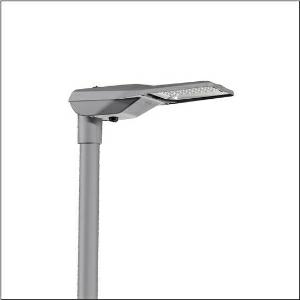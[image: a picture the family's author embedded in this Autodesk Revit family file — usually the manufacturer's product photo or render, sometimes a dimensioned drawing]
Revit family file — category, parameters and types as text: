
# Revit family: streetlight_sl_21_iq_mini___stw1_0a_5xe2e31y08gb_7efe
name_source: partatom
category: Lighting Fixtures
units: mm (PartAtom-declared; Revit-internal decimal feet)

## family parameters
Cut with Voids When Loaded = No
Host = Face
Light Source = No
Part Type = Normal
Room Calculation Point = No
Round Connector Dimension = Use Diameter
Shared = No

## types (1)
- --- (1 x LED, 5990 lm, 39.8 W, 3000K)
    Apparent Load = 40 VA
    CIE Flux Codes = 38 75 98 100 100
    Color Rendering = 70
    Color Temperature = 3000K
    Default Elevation = 1800 mm
    Description = Streetlight SL 21 iQ mini, mast luminaire, primary light control with lens, of PMMA, primary optical cover: cover, of toughened safety glass, transparent, light distribution: STW1.0a, light emission: direct distribution, primary light characteristic: asymmetric, installation type: post-top, side-entry, LED, High Power LED, rated luminous flux: 5.990lm, luminous efficacy: 151lm/W, light colour: 730, colour temperature: 3000K, control gear: iQ-Street Remote, D4i with power reduction, control: pre-setting: logarithmic dimming characteristic, Street-Remote, Auto-Match, Temp-Guard, Lumen-Switch, Night-Set, Smart-Wire, Light-Fading, Desk-Remote (wireless, voltage-free reading and setting of iQ features in the workshop via application-optimized NFC function/RFID function), optimised constant luminous flux control (CLO 2.0), mains connection: 220..240V, AC, 50/60Hz, start of lifetime: 40W, end of service life: 41W, reduction: 18W, luminaire housing, of diecast aluminium, powder-coated, Siteco® metallic grey (DB 702S), corrosivity category C5 mid according to DIN EN ISO 12944, please order mast flange separately, inclination adjustable: 0°, 5°, 10°, 15°, sealing non-destructively replaceable, multi-level sealing system, length: 628mm, width: 235mm, height: 110mm, mast flange for spigot size: 42mm (side-entry): 5XC10008XM4, 60/48mm (side-entry/post-top): 5XC10108XM2, 76/60mm (side-entry/post-top): 5XC10108XM1, mounting height: 4..8m, Smart Interface below and above, protection rating (complete): IP66, insulation class (complete): insulation class II (safety insulation), certification: CE, ENEC, ENEC+, VDE, impact resistance: IK10, permissible operating ambient temperature for outdoor applications: -40..+50°C, standard-compliant lighting for roads and squares, packaging unit: 1 piece

Light Distribution: STW1.0a
    Height = 110 mm
    Lamp = 1 x LED
    Lamp Light Flux = 5990 lm
    Lamp Power = 39.8 W
    Lamp count = 1
    Length = 625 mm
    Luminous efficacy = 151 lm/W
    Manufacturer = Siteco
    ModVariant = No
    Model = 5XE2E31Y08GB
    Number of Poles = 1
    OnlyDefault = Yes
    Power Factor = 1
    Product Name = Streetlight SL 21 iQ mini | STW1.0a
    Product group = mast luminaire | pylon top
    ProductGroupID = 6100
    Protection Class = Protection class II
    Protection Degree = IP 66
    RLX_Detail_Level = 1
    RLX_Emergency_Light_Flux = 0 lm
    RLX_Emergency_Type = 0
    RLX_Emergency_Type_DB = No
    RlxData = <blob elided: 26885 chars, md5=df0a2635>
    Socket = socket
    Standby Power = 0 W
    System Light Flux = 5990 lm
    System Power = 40 W
    Type Comments = factory setting: luminous flux: 100 % | dim-lin: 254 | 800 mA
    Type Image = l_1003514.jpg
    URL = http://relux.com
    VarID = @adj_114338
    Voltage = 0 V
    Weight = 0.00 kg
    Width = 234 mm

## geometry (parser evidence)
native form markers: Blend x4, Sweep x10
no freeform markers — native parametric forms only
